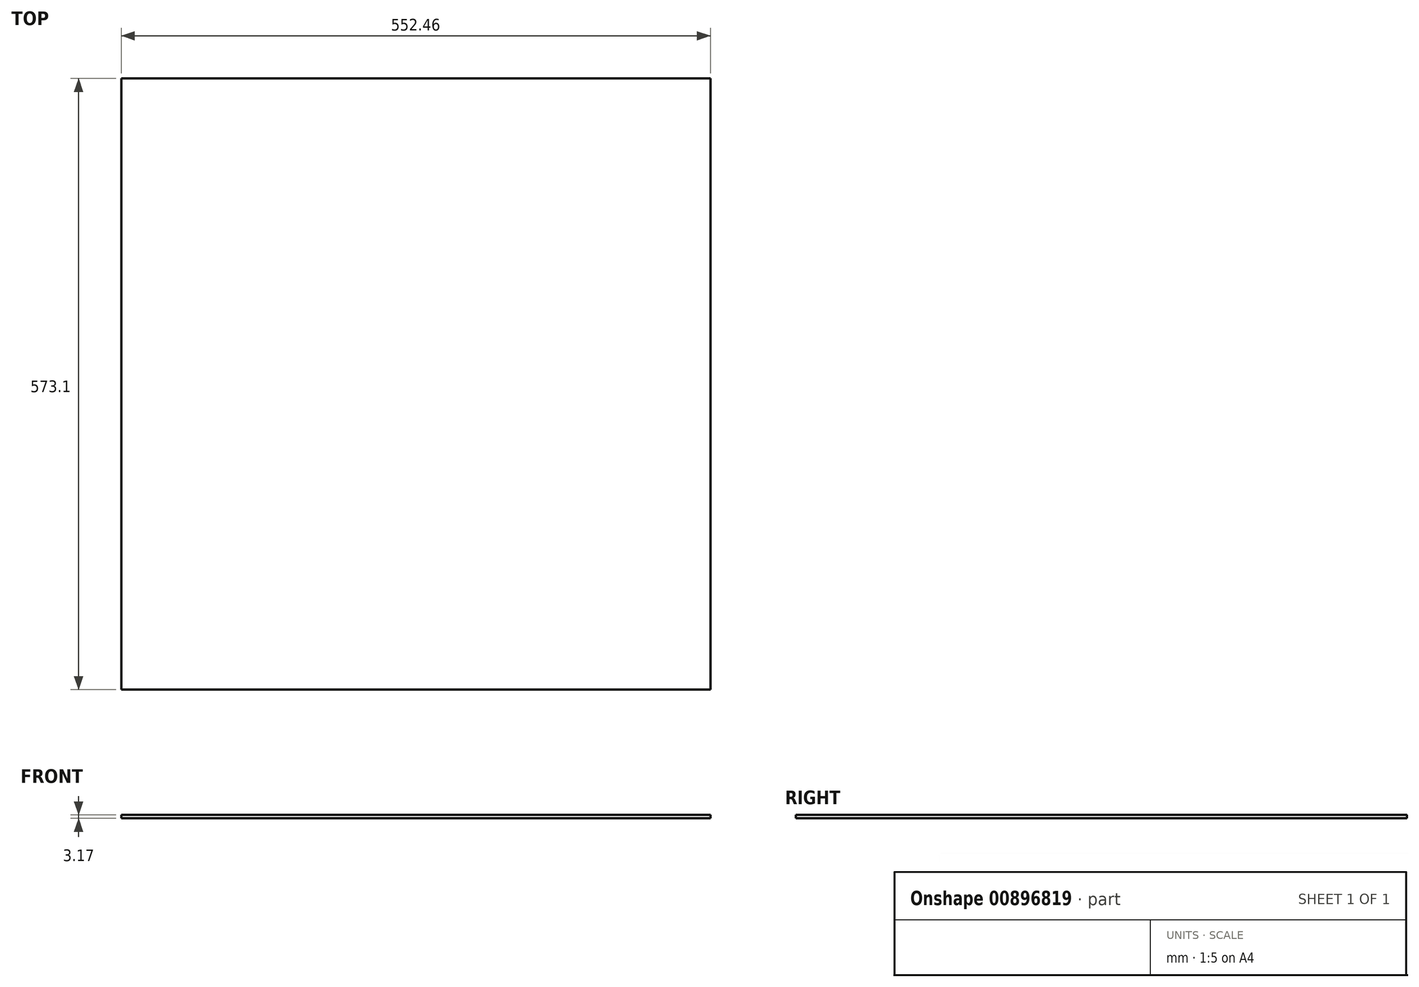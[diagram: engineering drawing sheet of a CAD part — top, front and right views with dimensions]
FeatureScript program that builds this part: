
annotation { "Feature Type Name" : "Feature", "Feature Type Description" : "" }
export const myFeature = defineFeature(function(context is Context, id is Id, definition is map)
    precondition{}
    {
        {
            var Q0;
            Q0=qCreatedBy(makeId("Top.planeOp"),FACE);
            var sketch = newSketch(context, id + "F0", { "sketchPlane" : qUnion([Q0])});
            skLineSegment(sketch, "E0.bottom", {"start": v(276.23, -286.55) * mm, "end": v(-276.23, -286.55) * mm});
            skLineSegment(sketch, "E0.top", {"start": v(276.23, 286.55) * mm, "end": v(-276.23, 286.55) * mm});
            skLineSegment(sketch, "E0.left", {"start": v(276.23, -286.55) * mm, "end": v(276.23, 286.55) * mm});
            skLineSegment(sketch, "E0.right", {"start": v(-276.23, -286.55) * mm, "end": v(-276.23, 286.55) * mm});
            skPoint(sketch, "E0.middle", {"position": v(0, 0) * mm});
            skSolve(sketch);
        }
        {
            var Q0;
            Q0 = qSketchRegion(id + "F0", true);
            extrude(context, id + "F1", {"entities" : qUnion([Q0]), "depth" : 3.17 * mm, "offsetDistance" : 25.4 * mm});
        }
    });
